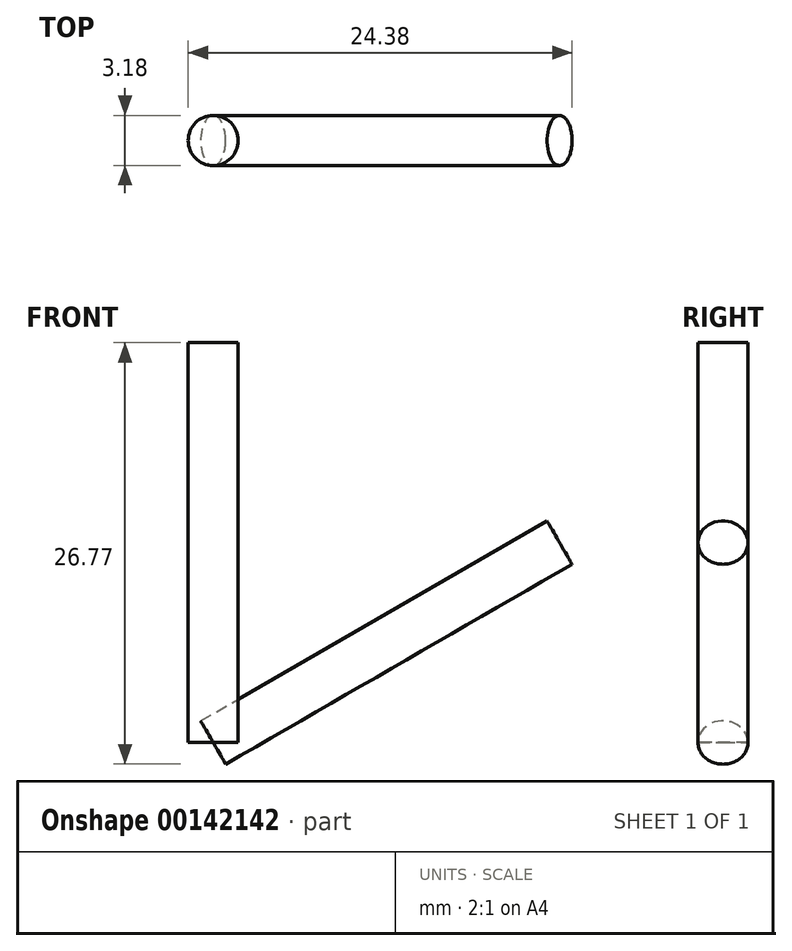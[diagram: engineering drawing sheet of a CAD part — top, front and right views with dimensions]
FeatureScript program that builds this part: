
annotation { "Feature Type Name" : "Feature", "Feature Type Description" : "" }
export const myFeature = defineFeature(function(context is Context, id is Id, definition is map)
    precondition{}
    {
        {
            var Q0;
            Q0=qCreatedBy(makeId("Front.planeOp"),FACE);
            var sketch = newSketch(context, id + "F0", { "sketchPlane" : qUnion([Q0])});
            skPoint(sketch, "E0", {"position": v(0, 0) * mm});
            skPoint(sketch, "E1", {"position": v(-0.15, 0.18) * mm});
            skLineSegment(sketch, "E2", {"start": v(0, 0) * mm, "end": v(0, 25.4) * mm});
            skSolve(sketch);
        }
        {
            var Q0;
            Q0=qCreatedBy(makeId("Top.planeOp"),FACE);
            var sketch = newSketch(context, id + "F1", { "sketchPlane" : qUnion([Q0])});
            skCircle(sketch, "E3", {"center": v(0, 0) * mm, "radius": 1.59 * mm});
            skLineSegment(sketch, "E4", {"start": v(0, 0) * mm, "end": v(0, 12.7) * mm});
            skSolve(sketch);
        }
        {
            var Q0;
            Q0=makeQuery(id+"F1.imprint","IMPRINT",FACE,{"disambiguationData":[TD([[makeQuery(id+"F1.imprint","IMPRINT",EDGE,{"derivedFrom":sQuery(id+"F1.wireOp",EDGE,"E3")}),1.0]])]});
            var Q1;
            Q1=sQuery(id+"F0.wireOp",EDGE,"E2");
            sweep(context, id + "F2", {"profiles" : qUnion([Q0]), "path" : qUnion([Q1])});
        }
        {
            var Q0;
            Q0=makeQuery(id+"F2.opSweep","SWEPT_BODY",BODY,{"disambiguationData":[OSD([sQuery(id+"F0.wireOp",EDGE,"E2"),sQuery(id+"F1.wireOp",EDGE,"E3")])]});
            var Q1;
            Q1=sQuery(id+"F1.wireOp",EDGE,"E4");
            transform(context, id + "F3", {"entities" : qUnion([Q0]), "transformType" : TransformType.ROTATION, "transformAxis" : qUnion([Q1]), "angle" : 60 * degree, "makeCopy" : true});
        }
    });
